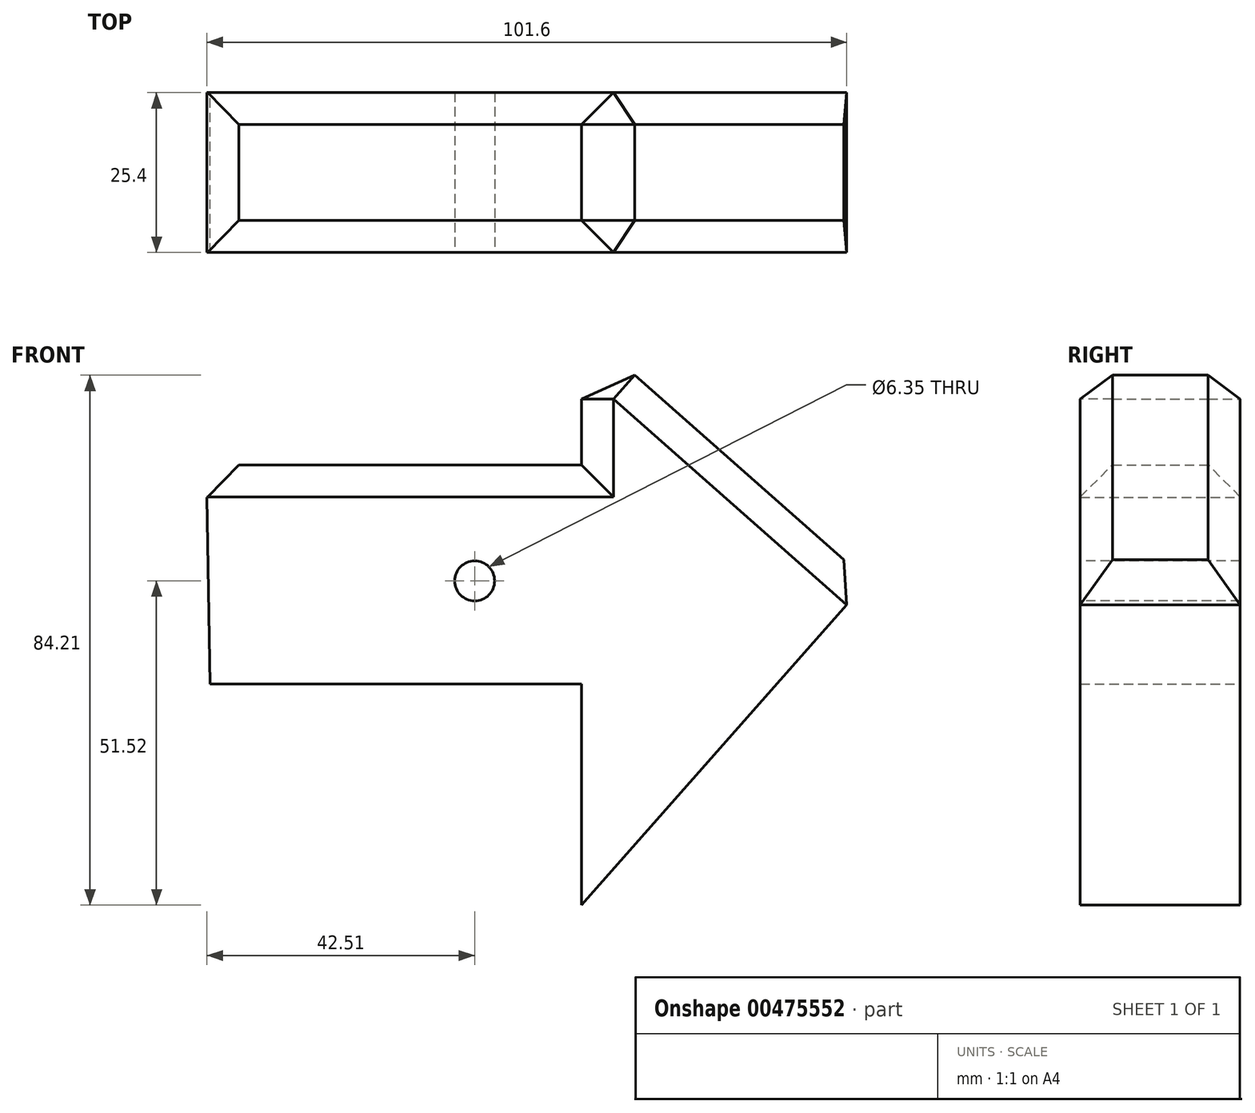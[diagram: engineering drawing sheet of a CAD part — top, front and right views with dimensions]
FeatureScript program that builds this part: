
annotation { "Feature Type Name" : "Feature", "Feature Type Description" : "" }
export const myFeature = defineFeature(function(context is Context, id is Id, definition is map)
    precondition{}
    {
        {
            var Q0;
            Q0=qCreatedBy(makeId("Front.planeOp"),FACE);
            var sketch = newSketch(context, id + "F0", { "sketchPlane" : qUnion([Q0])});
            skLineSegment(sketch, "E0", {"start": v(-42.02, -16.4) * mm, "end": v(16.98, -16.4) * mm});
            skLineSegment(sketch, "E1", {"start": v(16.98, -16.4) * mm, "end": v(16.98, -51.52) * mm});
            skLineSegment(sketch, "E2", {"start": v(16.98, -51.52) * mm, "end": v(62.45, 0) * mm});
            skLineSegment(sketch, "E3", {"start": v(62.45, 0) * mm, "end": v(16.98, 40.14) * mm});
            skLineSegment(sketch, "E4", {"start": v(16.98, 40.14) * mm, "end": v(16.98, 18.42) * mm});
            skLineSegment(sketch, "E5", {"start": v(16.98, 18.42) * mm, "end": v(-42.6, 18.42) * mm});
            skLineSegment(sketch, "E6", {"start": v(-42.6, 18.42) * mm, "end": v(-42.02, -16.4) * mm});
            skSolve(sketch);
        }
        {
            var Q0;
            Q0=makeQuery(id+"F0.imprint","IMPRINT",FACE,{"disambiguationData":[TD([[makeQuery(id+"F0.imprint","IMPRINT",EDGE,{"derivedFrom":sQuery(id+"F0.wireOp",EDGE,"E0")}),1.0]])]});
            extrude(context, id + "F1", {"entities" : qUnion([Q0]), "depth" : 25.4 * mm});
        }
        {
            var Q0;
            Q0=makeQuery(id+"F1.opExtrude","CAP_EDGE",EDGE,{"disambiguationData":[OSD([sQuery(id+"F0.wireOp",EDGE,"E3")])],"isStart":false});
            var Q1;
            Q1=makeQuery(id+"F1.opExtrude","CAP_EDGE",EDGE,{"disambiguationData":[OSD([sQuery(id+"F0.wireOp",EDGE,"E3")])],"isStart":true});
            var Q2;
            Q2=makeQuery(id+"F1.opExtrude","SWEPT_EDGE",EDGE,{"disambiguationData":[OSD([sQuery(id+"F0.wireOp",EDGE,"E3"),sQuery(id+"F0.wireOp",EDGE,"E4")])]});
            var Q3;
            Q3=makeQuery(id+"F1.opExtrude","SWEPT_EDGE",EDGE,{"disambiguationData":[OSD([sQuery(id+"F0.wireOp",EDGE,"E2"),sQuery(id+"F0.wireOp",EDGE,"E3")])]});
            var Q4;
            Q4=makeQuery(id+"F1.opExtrude","CAP_EDGE",EDGE,{"disambiguationData":[OSD([sQuery(id+"F0.wireOp",EDGE,"E5")])],"isStart":false});
            var Q5;
            Q5=makeQuery(id+"F1.opExtrude","CAP_EDGE",EDGE,{"disambiguationData":[OSD([sQuery(id+"F0.wireOp",EDGE,"E5")])],"isStart":true});
            var Q6;
            Q6=makeQuery(id+"F1.opExtrude","SWEPT_EDGE",EDGE,{"disambiguationData":[OSD([sQuery(id+"F0.wireOp",EDGE,"E5"),sQuery(id+"F0.wireOp",EDGE,"E6")])]});
            var Q7;
            Q7=makeQuery(id+"F1.opExtrude","CAP_EDGE",EDGE,{"disambiguationData":[OSD([sQuery(id+"F0.wireOp",EDGE,"E4")])],"isStart":false});
            var Q8;
            Q8=makeQuery(id+"F1.opExtrude","CAP_EDGE",EDGE,{"disambiguationData":[OSD([sQuery(id+"F0.wireOp",EDGE,"E4")])],"isStart":true});
            chamfer(context, id + "F2", {"entities" : qUnion([Q0, Q1, Q2, Q3, Q4, Q5, Q6, Q7, Q8]), "width" : 5.08 * mm, "tangentPropagation" : true});
        }
        {
            var Q0;
            Q0=makeQuery(id+"F1.opExtrude","CAP_FACE",FACE,{"disambiguationData":[OSD([sQuery(id+"F0.wireOp",EDGE,"E0"),sQuery(id+"F0.wireOp",EDGE,"E1"),sQuery(id+"F0.wireOp",EDGE,"E2"),sQuery(id+"F0.wireOp",EDGE,"E3"),sQuery(id+"F0.wireOp",EDGE,"E4"),sQuery(id+"F0.wireOp",EDGE,"E5"),sQuery(id+"F0.wireOp",EDGE,"E6")])],"isStart":false});
            var sketch = newSketch(context, id + "F3", { "sketchPlane" : qUnion([Q0])});
            skCircle(sketch, "E7", {"center": v(0, 0) * mm, "radius": 9.5 * mm});
            skSolve(sketch);
        }
        {
            var Q0;
            Q0=sQuery(id+"F3.wireOp",VERTEX,"E7.center");
            var Q1;
            Q1=makeQuery(id+"F1.opExtrude","SWEPT_BODY",BODY,{"disambiguationData":[OSD([sQuery(id+"F0.wireOp",EDGE,"E0"),sQuery(id+"F0.wireOp",EDGE,"E1"),sQuery(id+"F0.wireOp",EDGE,"E2"),sQuery(id+"F0.wireOp",EDGE,"E3"),sQuery(id+"F0.wireOp",EDGE,"E4"),sQuery(id+"F0.wireOp",EDGE,"E5"),sQuery(id+"F0.wireOp",EDGE,"E6")])]});
            hole(context, id + "F4", {"style" : HoleStyle.SIMPLE, "endStyle" : HoleEndStyle.THROUGH, "holeDiameter" : 6.35 * mm, "isTappedThrough" : true, "tappedDepth" : 12.7 * mm, "tapClearance" : 3, "locations" : qUnion([Q0]), "scope" : qUnion([Q1])});
        }
    });
